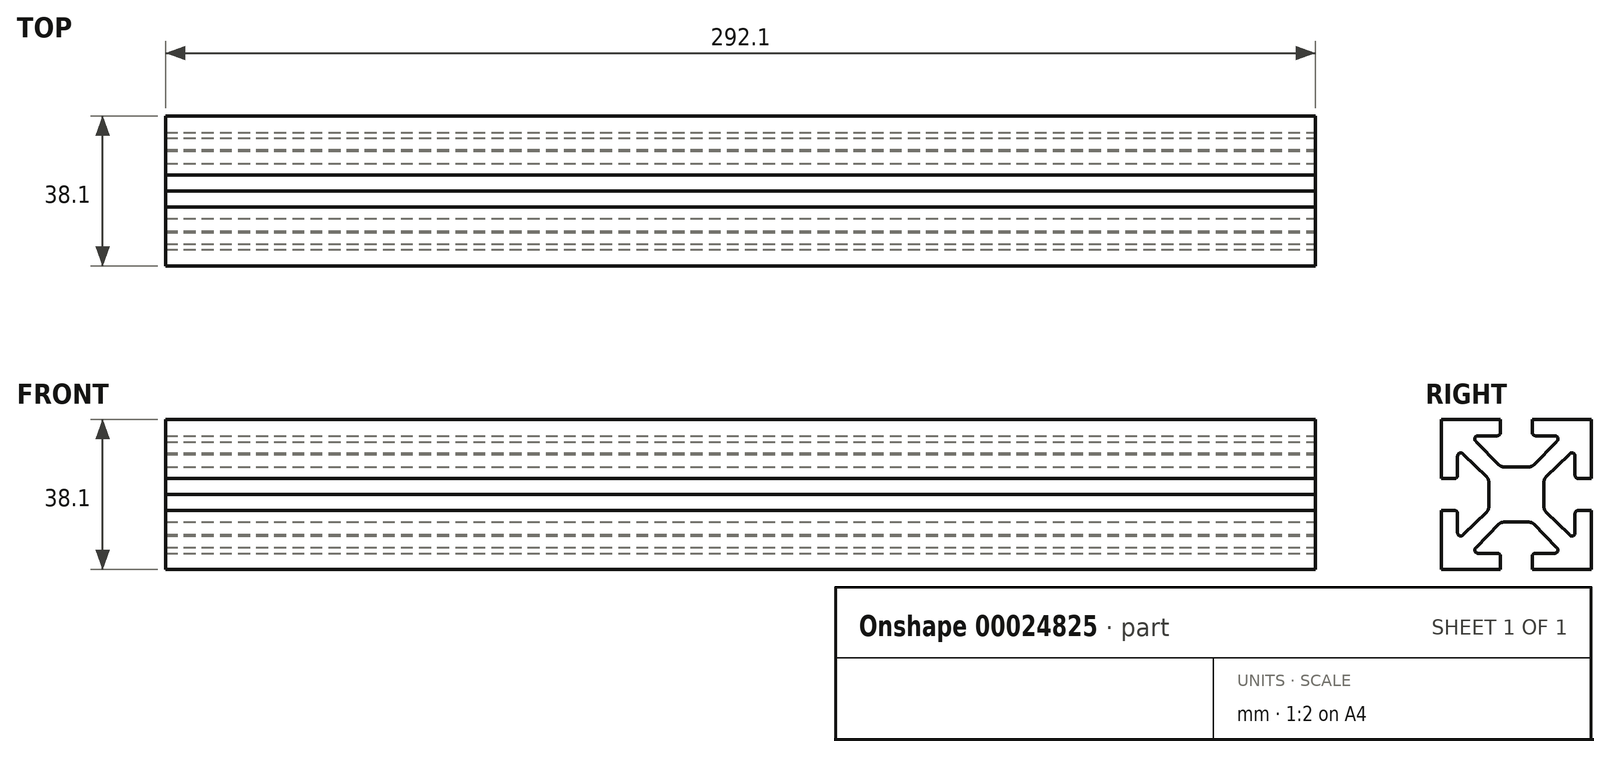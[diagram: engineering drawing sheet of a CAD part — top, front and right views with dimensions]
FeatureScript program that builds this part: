
annotation { "Feature Type Name" : "Feature", "Feature Type Description" : "" }
export const myFeature = defineFeature(function(context is Context, id is Id, definition is map)
    precondition{}
    {
        {
            var Q0;
            Q0=qCreatedBy(makeId("Right.planeOp"),FACE);
            var sketch = newSketch(context, id + "F0", { "sketchPlane" : qUnion([Q0])});
            skLineSegment(sketch, "E0.rect.bottom", {"start": v(19.05, 19.05) * mm, "end": v(-19.05, 19.05) * mm});
            skLineSegment(sketch, "E0.rect.top", {"start": v(19.05, -19.05) * mm, "end": v(-19.05, -19.05) * mm});
            skLineSegment(sketch, "E0.rect.left", {"start": v(19.05, 19.05) * mm, "end": v(19.05, -19.05) * mm});
            skLineSegment(sketch, "E0.rect.right", {"start": v(-19.05, 19.05) * mm, "end": v(-19.05, -19.05) * mm});
            skPoint(sketch, "E0.rect.middle", {"position": v(0, 0) * mm});
            skSolve(sketch);
        }
        {
            var Q0;
            Q0=makeQuery(id+"F0.imprint","IMPRINT",FACE,{"disambiguationData":[TD([[makeQuery(id+"F0.imprint","IMPRINT",EDGE,{"derivedFrom":sQuery(id+"F0.wireOp",EDGE,"E0.rect.bottom")}),1.0]])]});
            extrude(context, id + "F1", {"entities" : qUnion([Q0]), "endBound" : BoundingType.SYMMETRIC, "depth" : 292.1 * mm});
        }
        {
            var Q0;
            Q0=qCreatedBy(makeId("Right.planeOp"),FACE);
            var sketch = newSketch(context, id + "F2", { "sketchPlane" : qUnion([Q0])});
            skLineSegment(sketch, "E1", {"start": v(-4.06, 19.11) * mm, "end": v(-4.06, 15.71) * mm});
            skLineSegment(sketch, "E2", {"start": v(-4.86, 14.92) * mm, "end": v(-9.78, 14.92) * mm});
            skLineSegment(sketch, "E3", {"start": v(0, 6.99) * mm, "end": v(0, 19.05) * mm});
            skLineSegment(sketch, "E4", {"start": v(0, 19.05) * mm, "end": v(-4.06, 19.11) * mm});
            skPoint(sketch, "E5.visualSharp", {"position": v(-10.29, 14.92) * mm});
            skArc(sketch, "E5.filletArc", {"start": v(-9.78, 14.92) * mm, "mid": v(-10.56, 14.3) * mm, "end": v(-10.12, 13.4) * mm});
            skPoint(sketch, "E6.visualSharp", {"position": v(-4.06, 14.92) * mm});
            skArc(sketch, "E6.filletArc", {"start": v(-4.86, 14.92) * mm, "mid": v(-4.3, 15.15) * mm, "end": v(-4.06, 15.71) * mm});
            skLineSegment(sketch, "E7", {"start": v(-10.12, 13.4) * mm, "end": v(-4.4, 7.51) * mm});
            skLineSegment(sketch, "E8", {"start": v(-3.28, 7.03) * mm, "end": v(0, 6.99) * mm});
            skPoint(sketch, "E9.visualSharp", {"position": v(-3.94, 7.04) * mm});
            skArc(sketch, "E9.filletArc", {"start": v(-4.4, 7.51) * mm, "mid": v(-3.89, 7.16) * mm, "end": v(-3.28, 7.03) * mm});
            skLineSegment(sketch, "E10.1.0", {"start": v(6.99, 0) * mm, "end": v(19.05, 0) * mm});
            skArc(sketch, "E10.1.1", {"start": v(7.51, 4.4) * mm, "mid": v(7.16, 3.89) * mm, "end": v(7.03, 3.28) * mm});
            skLineSegment(sketch, "E10.1.2", {"start": v(14.92, 4.86) * mm, "end": v(14.92, 9.78) * mm});
            skLineSegment(sketch, "E10.1.3", {"start": v(19.11, 4.06) * mm, "end": v(15.71, 4.06) * mm});
            skLineSegment(sketch, "E10.1.4", {"start": v(19.05, 0) * mm, "end": v(19.11, 4.06) * mm});
            skLineSegment(sketch, "E10.1.5", {"start": v(7.03, 3.28) * mm, "end": v(6.99, 0) * mm});
            skLineSegment(sketch, "E10.1.6", {"start": v(13.4, 10.12) * mm, "end": v(7.51, 4.4) * mm});
            skArc(sketch, "E10.1.7", {"start": v(14.92, 4.86) * mm, "mid": v(15.15, 4.3) * mm, "end": v(15.71, 4.06) * mm});
            skArc(sketch, "E10.1.8", {"start": v(14.92, 9.78) * mm, "mid": v(14.3, 10.56) * mm, "end": v(13.4, 10.12) * mm});
            skLineSegment(sketch, "E10.2.0", {"start": v(0, -6.99) * mm, "end": v(0, -19.05) * mm});
            skArc(sketch, "E10.2.1", {"start": v(4.4, -7.51) * mm, "mid": v(3.89, -7.16) * mm, "end": v(3.28, -7.03) * mm});
            skLineSegment(sketch, "E10.2.2", {"start": v(4.86, -14.92) * mm, "end": v(9.78, -14.92) * mm});
            skLineSegment(sketch, "E10.2.3", {"start": v(4.06, -19.11) * mm, "end": v(4.06, -15.71) * mm});
            skLineSegment(sketch, "E10.2.4", {"start": v(0, -19.05) * mm, "end": v(4.06, -19.11) * mm});
            skLineSegment(sketch, "E10.2.5", {"start": v(3.28, -7.03) * mm, "end": v(0, -6.99) * mm});
            skLineSegment(sketch, "E10.2.6", {"start": v(10.12, -13.4) * mm, "end": v(4.4, -7.51) * mm});
            skArc(sketch, "E10.2.7", {"start": v(4.86, -14.92) * mm, "mid": v(4.3, -15.15) * mm, "end": v(4.06, -15.71) * mm});
            skArc(sketch, "E10.2.8", {"start": v(9.78, -14.92) * mm, "mid": v(10.56, -14.3) * mm, "end": v(10.12, -13.4) * mm});
            skPoint(sketch, "E10.center", {"position": v(0, 0) * mm});
            skLineSegment(sketch, "E10.anchor1", {"start": v(0, 0) * mm, "end": v(-10.12, 13.4) * mm, "construction": true});
            skLineSegment(sketch, "E10.anchor2", {"start": v(0, 0) * mm, "end": v(-13.4, -10.12) * mm, "construction": true});
            skArc(sketch, "E11.3.3.0", {"start": v(-7.51, -4.4) * mm, "mid": v(-7.16, -3.89) * mm, "end": v(-7.03, -3.28) * mm});
            skLineSegment(sketch, "E11.7.3.0", {"start": v(-14.92, -4.86) * mm, "end": v(-14.92, -9.78) * mm});
            skLineSegment(sketch, "E11.10.3.0", {"start": v(-19.11, -4.06) * mm, "end": v(-15.71, -4.06) * mm});
            skLineSegment(sketch, "E11.13.3.0", {"start": v(-19.05, 0) * mm, "end": v(-19.11, -4.06) * mm});
            skLineSegment(sketch, "E11.16.3.0", {"start": v(-7.03, -3.28) * mm, "end": v(-6.99, 0) * mm});
            skLineSegment(sketch, "E11.19.3.0", {"start": v(-13.4, -10.12) * mm, "end": v(-7.51, -4.4) * mm});
            skLineSegment(sketch, "E11.20.3.0", {"start": v(-6.99, 0) * mm, "end": v(-19.05, 0) * mm});
            skArc(sketch, "E11.22.3.0", {"start": v(-14.92, -4.86) * mm, "mid": v(-15.15, -4.3) * mm, "end": v(-15.71, -4.06) * mm});
            skArc(sketch, "E11.26.3.0", {"start": v(-14.92, -9.78) * mm, "mid": v(-14.3, -10.56) * mm, "end": v(-13.4, -10.12) * mm});
            skSolve(sketch);
        }
        {
            var Q0;
            Q0=qSketchRegion(id+"F2",true);
            extrude(context, id + "F3", {"entities" : qUnion([Q0]), "operationType" : NewBodyOperationType.REMOVE, "endBound" : BoundingType.SYMMETRIC, "oppositeDirection" : true, "depth" : 368.3 * mm});
        }
        {
            var Q0;
            Q0=makeQuery(id+"F1.opExtrude","SWEPT_BODY",BODY,{"disambiguationData":[OSD([sQuery(id+"F0.wireOp",EDGE,"E0.rect.bottom"),sQuery(id+"F0.wireOp",EDGE,"E0.rect.top"),sQuery(id+"F0.wireOp",EDGE,"E0.rect.left"),sQuery(id+"F0.wireOp",EDGE,"E0.rect.right")])]});
            var Q1;
            Q1=qCreatedBy(makeId("Front.planeOp"),FACE);
            mirror(context, id + "F4", {"operationType" : NewBodyOperationType.INTERSECT, "entities" : qUnion([Q0]), "mirrorPlane" : qUnion([Q1])});
        }
    });
